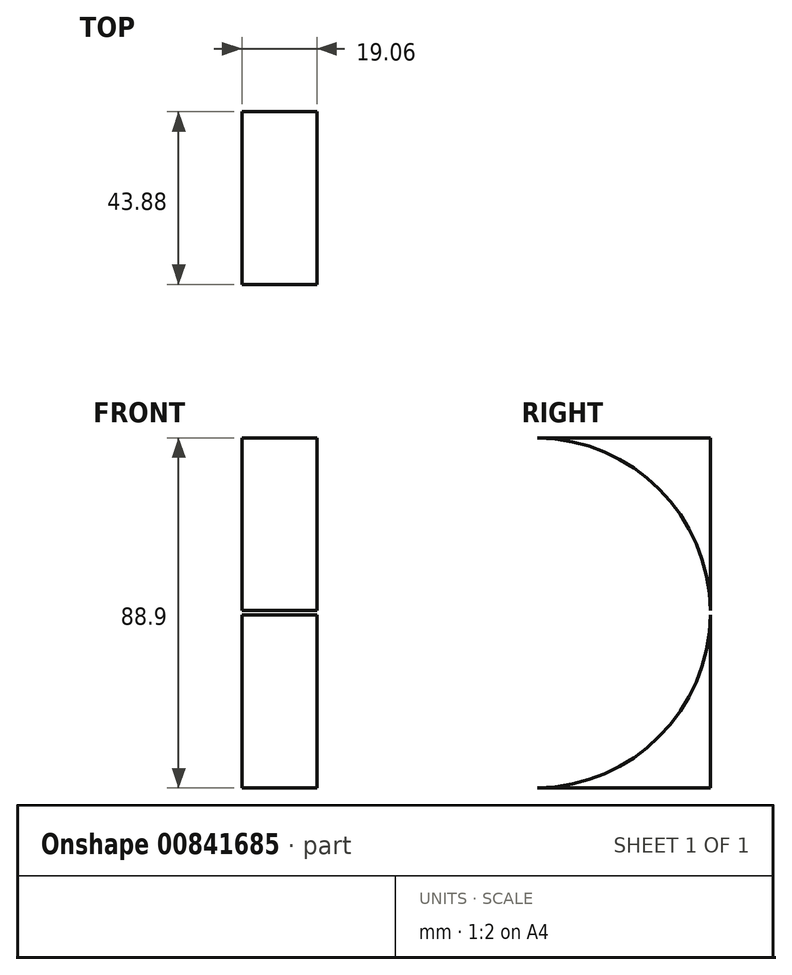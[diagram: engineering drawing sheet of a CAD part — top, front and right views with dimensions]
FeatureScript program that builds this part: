
annotation { "Feature Type Name" : "Feature", "Feature Type Description" : "" }
export const myFeature = defineFeature(function(context is Context, id is Id, definition is map)
    precondition{}
    {
        {
            var Q0;
            Q0=qCreatedBy(makeId("Front.planeOp"),FACE);
            var sketch = newSketch(context, id + "F0", { "sketchPlane" : qUnion([Q0])});
            skLineSegment(sketch, "E0.bottom", {"start": v(9.53, -44.45) * mm, "end": v(-9.52, -44.45) * mm});
            skLineSegment(sketch, "E0.top", {"start": v(9.53, 44.45) * mm, "end": v(-9.52, 44.45) * mm});
            skLineSegment(sketch, "E0.left", {"start": v(9.53, -44.45) * mm, "end": v(9.53, 44.45) * mm});
            skLineSegment(sketch, "E0.right", {"start": v(-9.52, -44.45) * mm, "end": v(-9.52, 44.45) * mm});
            skPoint(sketch, "E0.middle", {"position": v(0, 0) * mm});
            skSolve(sketch);
        }
        {
            var Q0;
            Q0 = qSketchRegion(id + "F0", true);
            extrude(context, id + "F1", {"entities" : qUnion([Q0]), "depth" : 304.8 * mm, "offsetDistance" : 25.4 * mm});
        }
        {
            var Q0;
            Q0=makeQuery(id+"F1.opExtrude","SWEPT_FACE",FACE,{"disambiguationData":[OSD([sQuery(id+"F0.wireOp",EDGE,"E0.left")])]});
            var sketch = newSketch(context, id + "F2", { "sketchPlane" : qUnion([Q0])});
            skLineSegment(sketch, "E1.bottom", {"start": v(-44.45, 44.45) * mm, "end": v(0, 44.45) * mm, "construction": true});
            skLineSegment(sketch, "E1.top", {"start": v(-44.45, 0) * mm, "end": v(0, 0) * mm, "construction": true});
            skLineSegment(sketch, "E1.left", {"start": v(-44.45, 44.45) * mm, "end": v(-44.45, 0) * mm, "construction": true});
            skLineSegment(sketch, "E1.right", {"start": v(0, 44.45) * mm, "end": v(0, 0) * mm, "construction": true});
            skSolve(sketch);
        }
        {
            var Q0;
            Q0=sQuery(id+"F2.wireOp",VERTEX,"E1.left.end");
            var Q1;
            Q1=makeQuery(id+"F1.opExtrude","SWEPT_BODY",BODY,{"disambiguationData":[OSD([sQuery(id+"F0.wireOp",EDGE,"E0.bottom"),sQuery(id+"F0.wireOp",EDGE,"E0.top"),sQuery(id+"F0.wireOp",EDGE,"E0.left"),sQuery(id+"F0.wireOp",EDGE,"E0.right")])]});
            hole(context, id + "F3", {"style" : HoleStyle.SIMPLE, "endStyle" : HoleEndStyle.THROUGH, "holeDiameter" : 6.35 * mm, "majorDiameter" : 6.35 * mm, "isTappedThrough" : true, "tappedDepth" : 12.7 * mm, "tapClearance" : 3, "locations" : qUnion([Q0]), "scope" : qUnion([Q1])});
        }
        {
            var Q0;
            Q0=makeQuery(id+"F1.opExtrude","SWEPT_FACE",FACE,{"disambiguationData":[OSD([sQuery(id+"F0.wireOp",EDGE,"E0.left")])]});
            var sketch = newSketch(context, id + "F4", { "sketchPlane" : qUnion([Q0])});
            skArc(sketch, "E2", {"start": v(-43.88, 44.45) * mm, "mid": v(0, -0.57) * mm, "end": v(-45.02, -44.45) * mm});
            skSolve(sketch);
        }
        {
            var Q0;
            {var subQ0=sQuery(id+"F4.wireOp",EDGE,"E2");var subQ1=sQuery(id+"F0.wireOp",EDGE,"E0.left");var subQ4=makeQuery(id+"F1.opExtrude","CAP_EDGE",EDGE,{"disambiguationData":[OSD([subQ1])],"isStart":true});var subQ5=makeQuery(id+"F4.imprint","INTERSECT",VERTEX,{"disambiguationData":[OD(0.0)],"derivedFrom":[subQ4,subQ0]});Q0=makeQuery(id+"F4.imprint","IMPRINT",FACE,{"disambiguationData":[TD([[makeQuery(id+"F4.imprint","IMPRINT",EDGE,{"disambiguationData":[TD([[subQ5,1.0]])],"derivedFrom":subQ0}),1.0]])]});}
            var Q1;
            {var subQ0=sQuery(id+"F4.wireOp",EDGE,"E2");var subQ1=sQuery(id+"F0.wireOp",EDGE,"E0.left");var subQ2=makeQuery(id+"F1.opExtrude","CAP_EDGE",EDGE,{"disambiguationData":[OSD([subQ1])],"isStart":true});var subQ3=makeQuery(id+"F4.imprint","INTERSECT",VERTEX,{"disambiguationData":[OD(1.0)],"derivedFrom":[subQ2,subQ0]});Q1=makeQuery(id+"F4.imprint","IMPRINT",FACE,{"disambiguationData":[TD([[makeQuery(id+"F4.imprint","IMPRINT",EDGE,{"disambiguationData":[TD([[subQ3,-1.0]])],"derivedFrom":subQ0}),1.0]])]});}
            extrude(context, id + "F5", {"entities" : qUnion([Q0, Q1]), "operationType" : NewBodyOperationType.REMOVE, "endBound" : BoundingType.THROUGH_ALL, "oppositeDirection" : true, "depth" : 25.4 * mm, "offsetDistance" : 25.4 * mm});
        }
    });
